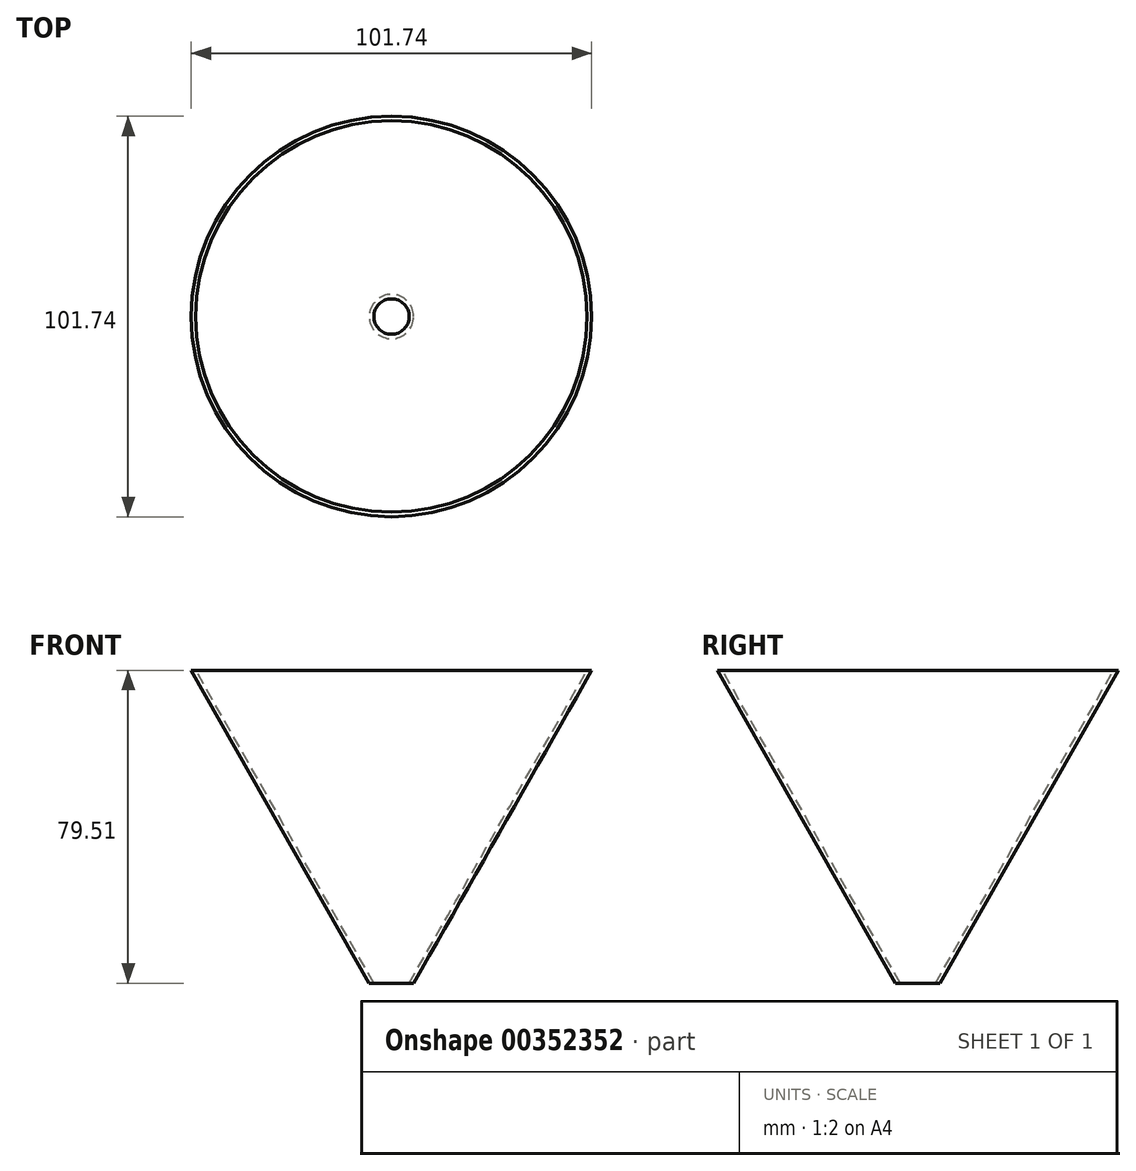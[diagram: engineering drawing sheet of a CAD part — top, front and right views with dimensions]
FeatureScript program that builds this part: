
annotation { "Feature Type Name" : "Feature", "Feature Type Description" : "" }
export const myFeature = defineFeature(function(context is Context, id is Id, definition is map)
    precondition{}
    {
        {
            var Q0;
            Q0=qCreatedBy(makeId("Front.planeOp"),FACE);
            var sketch = newSketch(context, id + "F0", { "sketchPlane" : qUnion([Q0])});
            skLineSegment(sketch, "E0", {"start": v(4.5, 0) * mm, "end": v(49.72, 79.5) * mm});
            skLineSegment(sketch, "E1.0", {"start": v(5.65, 0) * mm, "end": v(50.87, 79.5) * mm});
            skLineSegment(sketch, "E2", {"start": v(4.5, 0) * mm, "end": v(5.65, 0) * mm});
            skLineSegment(sketch, "E3", {"start": v(50.87, 79.5) * mm, "end": v(49.72, 79.5) * mm});
            skPoint(sketch, "E4.orphan", {"position": v(50, 80) * mm});
            skSolve(sketch);
        }
        {
            var Q0;
            Q0=qCreatedBy(makeId("Front.planeOp"),FACE);
            var sketch = newSketch(context, id + "F1", { "sketchPlane" : qUnion([Q0])});
            skLineSegment(sketch, "E5", {"start": v(0, 79.73) * mm, "end": v(0, -29.31) * mm, "construction": true});
            skSolve(sketch);
        }
        {
            var Q0;
            Q0=makeQuery(id+"F0.imprint","IMPRINT",FACE,{"disambiguationData":[TD([[makeQuery(id+"F0.imprint","IMPRINT",EDGE,{"derivedFrom":sQuery(id+"F0.wireOp",EDGE,"E0")}),-1.0]])]});
            var Q1;
            Q1=sQuery(id+"F1.wireOp",EDGE,"E5");
            revolve(context, id + "F2", {"entities" : qUnion([Q0]), "axis" : qUnion([Q1]), "revolveType" : RevolveType.FULL});
        }
    });
